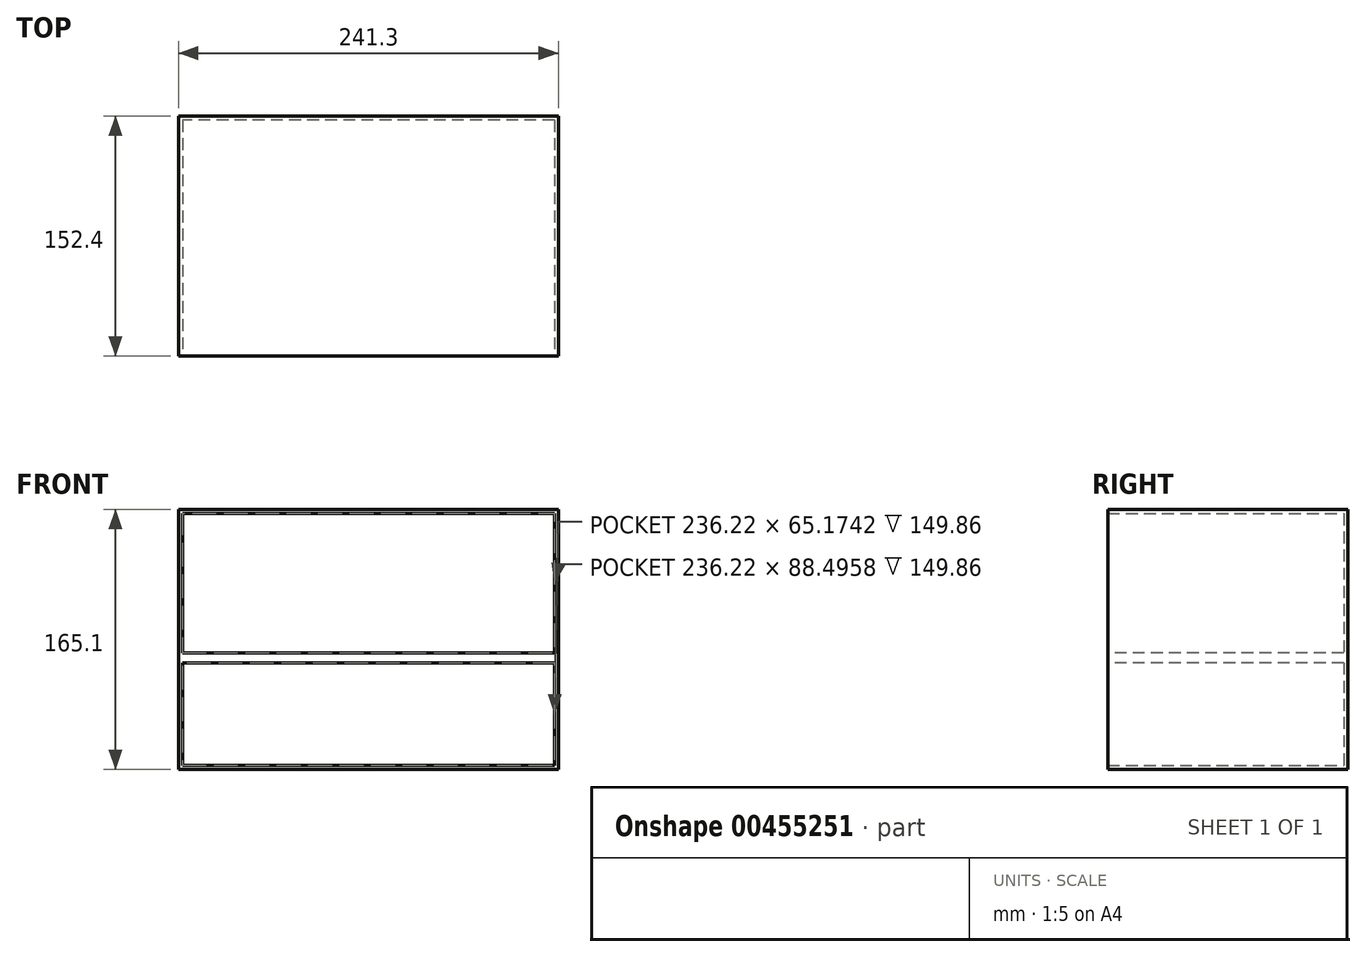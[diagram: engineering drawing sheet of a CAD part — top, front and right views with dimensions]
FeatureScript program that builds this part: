
annotation { "Feature Type Name" : "Feature", "Feature Type Description" : "" }
export const myFeature = defineFeature(function(context is Context, id is Id, definition is map)
    precondition{}
    {
        {
            var Q0;
            Q0=qCreatedBy(makeId("Front.planeOp"),FACE);
            var sketch = newSketch(context, id + "F0", { "sketchPlane" : qUnion([Q0])});
            skLineSegment(sketch, "E0.bottom", {"start": v(-125.01, 97.39) * mm, "end": v(116.29, 97.39) * mm});
            skLineSegment(sketch, "E0.top", {"start": v(-125.01, -67.71) * mm, "end": v(116.29, -67.71) * mm});
            skLineSegment(sketch, "E0.left", {"start": v(-125.01, 97.39) * mm, "end": v(-125.01, -67.71) * mm});
            skLineSegment(sketch, "E0.right", {"start": v(116.29, 97.39) * mm, "end": v(116.29, -67.71) * mm});
            skSolve(sketch);
        }
        {
            var Q0;
            Q0=makeQuery(id+"F0.imprint","IMPRINT",FACE,{"disambiguationData":[TD([[makeQuery(id+"F0.imprint","IMPRINT",EDGE,{"derivedFrom":sQuery(id+"F0.wireOp",EDGE,"E0.bottom")}),-1.0]])]});
            extrude(context, id + "F1", {"entities" : qUnion([Q0]), "depth" : 152.4 * mm});
        }
        {
            var Q0;
            Q0=makeQuery(id+"F1.opExtrude","CAP_FACE",FACE,{"disambiguationData":[OSD([sQuery(id+"F0.wireOp",EDGE,"E0.bottom"),sQuery(id+"F0.wireOp",EDGE,"E0.top"),sQuery(id+"F0.wireOp",EDGE,"E0.left"),sQuery(id+"F0.wireOp",EDGE,"E0.right")])],"isStart":false});
            shell(context, id + "F2", {"entities" : qUnion([Q0]), "thickness" : 2.54 * mm});
        }
        {
            var Q0;
            Q0=qCreatedBy(makeId("Top.planeOp"),FACE);
            var sketch = newSketch(context, id + "F3", { "sketchPlane" : qUnion([Q0])});
            skLineSegment(sketch, "E1.bottom", {"start": v(113.92, 0) * mm, "end": v(-123.57, 0) * mm});
            skLineSegment(sketch, "E1.top", {"start": v(113.92, -152.4) * mm, "end": v(-123.57, -152.4) * mm});
            skLineSegment(sketch, "E1.left", {"start": v(113.92, 0) * mm, "end": v(113.92, -152.4) * mm});
            skLineSegment(sketch, "E1.right", {"start": v(-123.57, 0) * mm, "end": v(-123.57, -152.4) * mm});
            skSolve(sketch);
        }
        {
            var Q0;
            Q0 = qSketchRegion(id + "F3", true);
            extrude(context, id + "F4", {"entities" : qUnion([Q0]), "operationType" : NewBodyOperationType.ADD, "depth" : 6.35 * mm});
        }
    });
